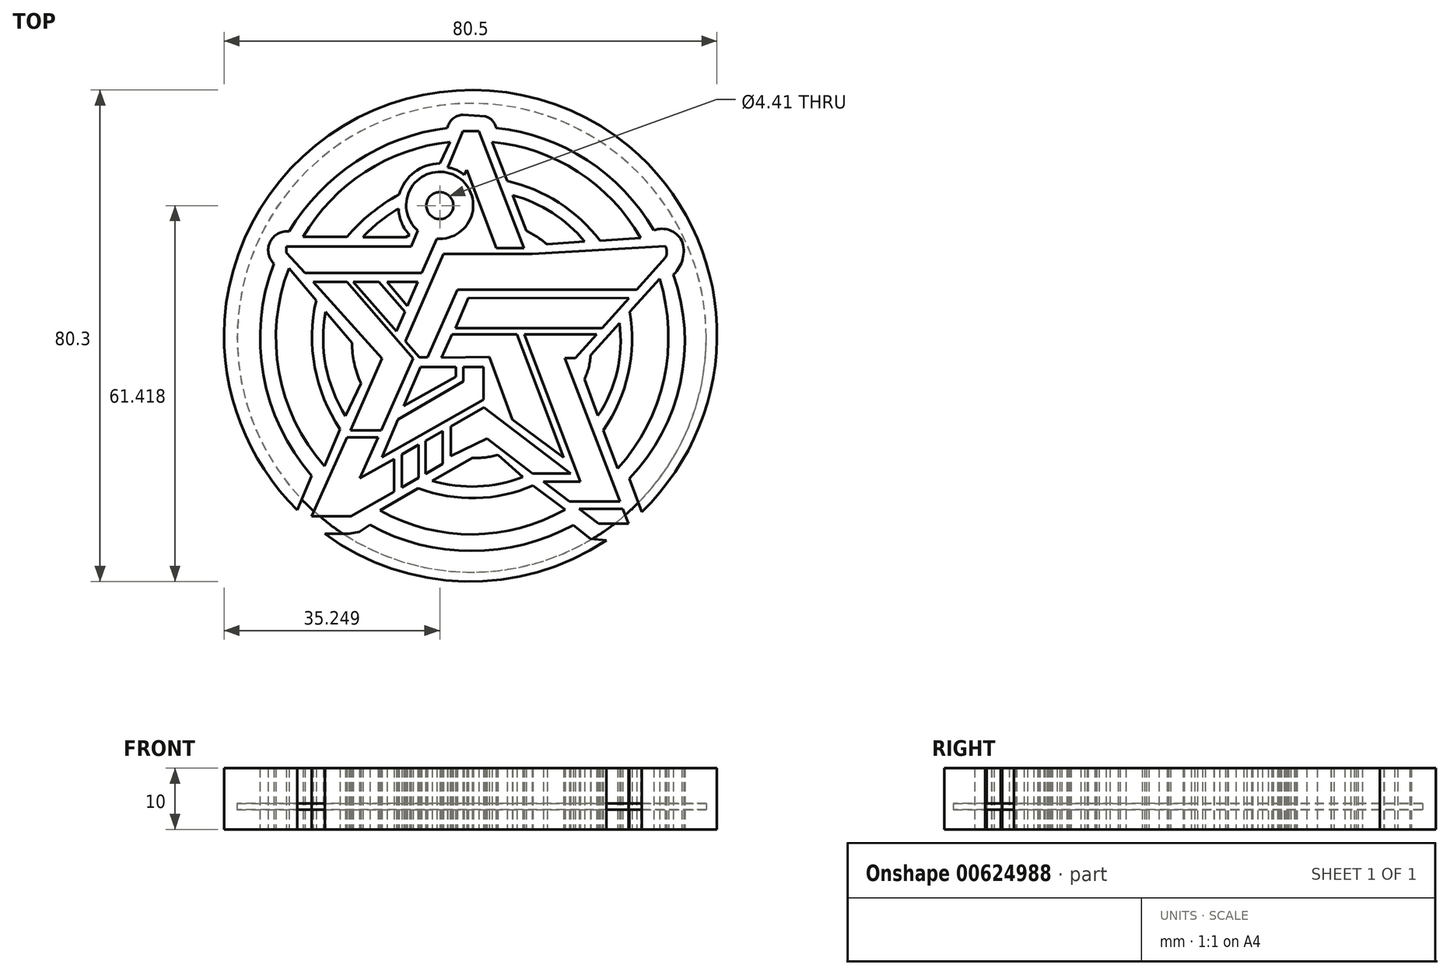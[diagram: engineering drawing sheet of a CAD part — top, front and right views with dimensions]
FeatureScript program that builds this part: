
annotation { "Feature Type Name" : "Feature", "Feature Type Description" : "" }
export const myFeature = defineFeature(function(context is Context, id is Id, definition is map)
    precondition{}
    {
        {
            var Q0;
            Q0=qCreatedBy(makeId("Top.planeOp"),FACE);
            var sketch = newSketch(context, id + "F0", { "sketchPlane" : qUnion([Q0])});
            skCircle(sketch, "E0", {"center": v(0, 0) * mm, "radius": 19.62 * mm, "construction": true});
            skCircle(sketch, "E1", {"center": v(0, 0) * mm, "radius": 24.24 * mm, "construction": true});
            skCircle(sketch, "E2", {"center": v(0, 0) * mm, "radius": 34.5 * mm, "construction": true});
            skLineSegment(sketch, "E3", {"start": v(20.7, -30.4) * mm, "end": v(2.49, -16.49) * mm, "construction": true});
            skLineSegment(sketch, "E4", {"start": v(2.49, -16.49) * mm, "end": v(-19.72, -29.2) * mm, "construction": true});
            skLineSegment(sketch, "E5", {"start": v(2, -11.38) * mm, "end": v(-18.24, -22.97) * mm, "construction": true});
            skLineSegment(sketch, "E6", {"start": v(-18.24, -22.97) * mm, "end": v(-9.56, -3.39) * mm, "construction": true});
            skLineSegment(sketch, "E7", {"start": v(-5.7, 16.2) * mm, "end": v(-12.28, 1.1) * mm, "construction": true});
            skLineSegment(sketch, "E8", {"start": v(-25.9, 9.11) * mm, "end": v(-8.79, 9.11) * mm, "construction": true});
            skLineSegment(sketch, "E9", {"start": v(23.83, -21.37) * mm, "end": v(18.4, -6.8) * mm, "construction": true});
            skLineSegment(sketch, "E10", {"start": v(30.66, 9.62) * mm, "end": v(19.42, -2.8) * mm, "construction": true});
            skLineSegment(sketch, "E11", {"start": v(25.58, -30.36) * mm, "end": v(15.19, -3.34) * mm, "construction": true});
            skLineSegment(sketch, "E12", {"start": v(15.19, -3.34) * mm, "end": v(16.91, -3.34) * mm, "construction": true});
            skLineSegment(sketch, "E13", {"start": v(16.91, -3.34) * mm, "end": v(31.66, 13.12) * mm, "construction": true});
            skLineSegment(sketch, "E14", {"start": v(27.56, 16.32) * mm, "end": v(12.3, 15.29) * mm, "construction": true});
            skLineSegment(sketch, "E15", {"start": v(3.31, 32) * mm, "end": v(8.9, 17.49) * mm, "construction": true});
            skArc(sketch, "E16", {"start": v(12.3, 15.29) * mm, "mid": v(10.66, 16.48) * mm, "end": v(8.9, 17.49) * mm});
            skArc(sketch, "E17", {"start": v(18.46, 15.7) * mm, "mid": v(13.15, 20.41) * mm, "end": v(6.66, 23.3) * mm});
            skArc(sketch, "E18", {"start": v(20.95, 15.87) * mm, "mid": v(14.22, 22.1) * mm, "end": v(5.77, 25.62) * mm});
            skArc(sketch, "E19", {"start": v(27.56, 16.32) * mm, "mid": v(17.36, 27.13) * mm, "end": v(3.31, 32) * mm});
            skLineSegment(sketch, "E20", {"start": v(3.31, 32) * mm, "end": v(5.77, 25.62) * mm});
            skLineSegment(sketch, "E21", {"start": v(6.66, 23.3) * mm, "end": v(8.9, 17.49) * mm});
            skLineSegment(sketch, "E22", {"start": v(12.3, 15.29) * mm, "end": v(18.46, 15.7) * mm});
            skLineSegment(sketch, "E23", {"start": v(20.95, 15.87) * mm, "end": v(27.56, 16.32) * mm});
            skLineSegment(sketch, "E24", {"start": v(-3.92, 27.8) * mm, "end": v(-1.42, 33.75) * mm});
            skLineSegment(sketch, "E25", {"start": v(-1.42, 33.75) * mm, "end": v(1.17, 33.75) * mm});
            skLineSegment(sketch, "E26", {"start": v(1.17, 33.75) * mm, "end": v(8.52, 14.66) * mm});
            skLineSegment(sketch, "E27", {"start": v(8.52, 14.66) * mm, "end": v(4.02, 14.66) * mm});
            skLineSegment(sketch, "E28", {"start": v(4.02, 14.66) * mm, "end": v(-0.78, 27.44) * mm});
            skLineSegment(sketch, "E29", {"start": v(-0.78, 27.44) * mm, "end": v(-1.24, 26.58) * mm});
            skArc(sketch, "E30", {"start": v(-1.24, 26.58) * mm, "mid": v(-2.48, 27.41) * mm, "end": v(-3.92, 27.8) * mm});
            skCircle(sketch, "E31", {"center": v(-5.21, 21.6) * mm, "radius": 2.2 * mm});
            skLineSegment(sketch, "E32", {"start": v(-5.7, 16.2) * mm, "end": v(-8.16, 10.56) * mm});
            skLineSegment(sketch, "E33", {"start": v(-8.16, 10.56) * mm, "end": v(-27.23, 10.56) * mm});
            skLineSegment(sketch, "E34", {"start": v(-27.23, 10.56) * mm, "end": v(-30.3, 13.9) * mm});
            skLineSegment(sketch, "E35", {"start": v(-30.3, 13.9) * mm, "end": v(-30.3, 14.9) * mm});
            skLineSegment(sketch, "E36", {"start": v(-30.3, 14.9) * mm, "end": v(-9.9, 14.9) * mm});
            skLineSegment(sketch, "E37", {"start": v(-9.9, 14.9) * mm, "end": v(-8.78, 17.49) * mm});
            skArc(sketch, "E38", {"start": v(-5.7, 16.2) * mm, "mid": v(-3.11, 26.69) * mm, "end": v(-8.78, 17.49) * mm});
            skLineSegment(sketch, "E39", {"start": v(-10.79, 16.46) * mm, "end": v(-10.16, 16.79) * mm});
            skLineSegment(sketch, "E40", {"start": v(-10.79, 16.46) * mm, "end": v(-17.8, 16.46) * mm});
            skArc(sketch, "E41", {"start": v(-11.95, 21.09) * mm, "mid": v(-15.04, 18.99) * mm, "end": v(-17.8, 16.46) * mm});
            skArc(sketch, "E42", {"start": v(-11.95, 21.09) * mm, "mid": v(-11.44, 18.78) * mm, "end": v(-10.16, 16.79) * mm});
            skArc(sketch, "E43", {"start": v(-5.2, 28.49) * mm, "mid": v(-9.36, 27.06) * mm, "end": v(-11.83, 23.42) * mm});
            skLineSegment(sketch, "E44", {"start": v(-5.2, 28.49) * mm, "end": v(-3.52, 32.02) * mm});
            skLineSegment(sketch, "E45", {"start": v(-20.38, 16.47) * mm, "end": v(-27.54, 16.47) * mm});
            skArc(sketch, "E46", {"start": v(-3.52, 32.02) * mm, "mid": v(-17.38, 27.1) * mm, "end": v(-27.54, 16.47) * mm});
            skArc(sketch, "E47", {"start": v(-11.83, 23.42) * mm, "mid": v(-16.43, 20.34) * mm, "end": v(-20.38, 16.47) * mm});
            skLineSegment(sketch, "E48", {"start": v(-13.82, 9.11) * mm, "end": v(-10.5, 5.18) * mm});
            skLineSegment(sketch, "E49", {"start": v(-10.5, 5.18) * mm, "end": v(-8.79, 9.11) * mm});
            skLineSegment(sketch, "E50", {"start": v(-13.82, 9.11) * mm, "end": v(-8.79, 9.11) * mm});
            skLineSegment(sketch, "E51", {"start": v(-19.38, 9.11) * mm, "end": v(-15.15, 9.11) * mm});
            skLineSegment(sketch, "E52", {"start": v(-15.15, 9.11) * mm, "end": v(-10.91, 4.22) * mm});
            skLineSegment(sketch, "E53", {"start": v(-10.91, 4.22) * mm, "end": v(-12.28, 1.1) * mm});
            skLineSegment(sketch, "E54", {"start": v(-12.28, 1.1) * mm, "end": v(-19.38, 9.11) * mm});
            skLineSegment(sketch, "E55", {"start": v(-25.9, 9.11) * mm, "end": v(-20.34, 9.11) * mm});
            skLineSegment(sketch, "E56", {"start": v(-20.34, 9.11) * mm, "end": v(-9.56, -3.39) * mm});
            skLineSegment(sketch, "E57", {"start": v(-9.56, -3.39) * mm, "end": v(-14.76, -15.11) * mm});
            skLineSegment(sketch, "E58", {"start": v(-14.76, -15.11) * mm, "end": v(-19.82, -15.11) * mm});
            skLineSegment(sketch, "E59", {"start": v(-19.82, -15.11) * mm, "end": v(-14.62, -3.39) * mm});
            skLineSegment(sketch, "E60", {"start": v(-14.62, -3.39) * mm, "end": v(-25.9, 9.11) * mm});
            skLineSegment(sketch, "E61", {"start": v(-7.25, -3.18) * mm, "end": v(-8.54, -3.18) * mm});
            skLineSegment(sketch, "E62", {"start": v(-8.54, -3.18) * mm, "end": v(-10.84, -0.58) * mm});
            skLineSegment(sketch, "E63", {"start": v(-10.84, -0.58) * mm, "end": v(-4.63, 13.7) * mm});
            skLineSegment(sketch, "E64", {"start": v(-4.63, 13.7) * mm, "end": v(9.88, 13.7) * mm});
            skLineSegment(sketch, "E65", {"start": v(9.88, 13.7) * mm, "end": v(31.6, 14.98) * mm});
            skLineSegment(sketch, "E66", {"start": v(31.66, 13.12) * mm, "end": v(26.93, 7.84) * mm});
            skLineSegment(sketch, "E67", {"start": v(26.93, 7.84) * mm, "end": v(-2.35, 7.84) * mm});
            skLineSegment(sketch, "E68", {"start": v(-2.35, 7.84) * mm, "end": v(-7.25, -3.18) * mm});
            skArc(sketch, "E69", {"start": v(31.66, 13.12) * mm, "mid": v(31.86, 14.06) * mm, "end": v(31.6, 14.98) * mm});
            skLineSegment(sketch, "E70", {"start": v(25.68, 6.44) * mm, "end": v(21.3, 1.56) * mm});
            skLineSegment(sketch, "E71", {"start": v(21.3, 1.56) * mm, "end": v(-2.63, 1.56) * mm});
            skLineSegment(sketch, "E72", {"start": v(-0.54, 6.55) * mm, "end": v(-4.93, -3.25) * mm, "construction": true});
            skLineSegment(sketch, "E73", {"start": v(1.9, -4.77) * mm, "end": v(-8.37, -4.77) * mm, "construction": true});
            skLineSegment(sketch, "E74", {"start": v(-8.37, -4.77) * mm, "end": v(-14.63, -19.5) * mm, "construction": true});
            skLineSegment(sketch, "E75", {"start": v(-11.07, -11.11) * mm, "end": v(-2.59, -6.39) * mm});
            skLineSegment(sketch, "E76", {"start": v(-2.59, -6.39) * mm, "end": v(-2.59, -4.77) * mm});
            skLineSegment(sketch, "E77", {"start": v(-2.59, -4.77) * mm, "end": v(-8.37, -4.77) * mm});
            skLineSegment(sketch, "E78", {"start": v(-11.07, -11.11) * mm, "end": v(-8.37, -4.77) * mm});
            skLineSegment(sketch, "E79", {"start": v(-1.37, -4.77) * mm, "end": v(1.9, -4.77) * mm});
            skLineSegment(sketch, "E80", {"start": v(1.9, -10.12) * mm, "end": v(1.9, -4.77) * mm});
            skLineSegment(sketch, "E81", {"start": v(1.9, -10.12) * mm, "end": v(-14.63, -19.5) * mm});
            skLineSegment(sketch, "E82", {"start": v(-1.37, -4.77) * mm, "end": v(-1.37, -7.1) * mm});
            skLineSegment(sketch, "E83", {"start": v(-1.37, -7.1) * mm, "end": v(-12.03, -13.38) * mm});
            skLineSegment(sketch, "E84", {"start": v(-12.03, -13.38) * mm, "end": v(-14.63, -19.5) * mm});
            skLineSegment(sketch, "E85", {"start": v(20.38, 0.53) * mm, "end": v(-3.24, 0.53) * mm, "construction": true});
            skLineSegment(sketch, "E86", {"start": v(-3.24, 0.53) * mm, "end": v(7.4, 0.53) * mm});
            skLineSegment(sketch, "E87", {"start": v(7.4, 0.53) * mm, "end": v(14.97, -19.6) * mm});
            skLineSegment(sketch, "E88", {"start": v(14.97, -19.6) * mm, "end": v(6.62, -13.36) * mm});
            skLineSegment(sketch, "E89", {"start": v(6.62, -13.36) * mm, "end": v(2.87, -3.12) * mm});
            skLineSegment(sketch, "E90", {"start": v(2.87, -3.12) * mm, "end": v(-4.93, -3.25) * mm});
            skLineSegment(sketch, "E91", {"start": v(-4.93, -3.25) * mm, "end": v(-3.24, 0.53) * mm});
            skLineSegment(sketch, "E92", {"start": v(20.38, 0.53) * mm, "end": v(8.57, 0.53) * mm});
            skLineSegment(sketch, "E93", {"start": v(8.57, 0.53) * mm, "end": v(17.74, -23.52) * mm});
            skLineSegment(sketch, "E94", {"start": v(17.74, -23.52) * mm, "end": v(11.7, -23.52) * mm});
            skLineSegment(sketch, "E95", {"start": v(11.7, -23.52) * mm, "end": v(15.95, -26.77) * mm});
            skLineSegment(sketch, "E96", {"start": v(15.95, -26.77) * mm, "end": v(24.2, -26.77) * mm});
            skLineSegment(sketch, "E97", {"start": v(24.2, -26.77) * mm, "end": v(15.19, -3.34) * mm});
            skLineSegment(sketch, "E98", {"start": v(15.19, -3.34) * mm, "end": v(16.91, -3.34) * mm});
            skLineSegment(sketch, "E99", {"start": v(16.91, -3.34) * mm, "end": v(20.38, 0.53) * mm});
            skLineSegment(sketch, "E100", {"start": v(-2.63, 1.56) * mm, "end": v(-0.54, 6.55) * mm});
            skLineSegment(sketch, "E101", {"start": v(-0.54, 6.55) * mm, "end": v(25.68, 6.44) * mm});
            skArc(sketch, "E102", {"start": v(18.4, -6.8) * mm, "mid": v(19.1, -4.85) * mm, "end": v(19.42, -2.8) * mm});
            skArc(sketch, "E103", {"start": v(20.62, -12.74) * mm, "mid": v(23.74, -5.5) * mm, "end": v(24.12, 2.38) * mm});
            skArc(sketch, "E104", {"start": v(21.5, -15.12) * mm, "mid": v(25.55, -5.86) * mm, "end": v(25.8, 4.24) * mm});
            skArc(sketch, "E105", {"start": v(23.83, -21.37) * mm, "mid": v(31.37, -6.79) * mm, "end": v(30.66, 9.62) * mm});
            skLineSegment(sketch, "E106", {"start": v(30.66, 9.62) * mm, "end": v(25.8, 4.24) * mm});
            skLineSegment(sketch, "E107", {"start": v(24.12, 2.38) * mm, "end": v(19.42, -2.8) * mm});
            skLineSegment(sketch, "E108", {"start": v(18.4, -6.8) * mm, "end": v(20.62, -12.74) * mm});
            skLineSegment(sketch, "E109", {"start": v(21.5, -15.12) * mm, "end": v(23.83, -21.37) * mm});
            skLineSegment(sketch, "E110", {"start": v(17.52, -27.97) * mm, "end": v(24.66, -27.97) * mm});
            skLineSegment(sketch, "E111", {"start": v(24.66, -27.97) * mm, "end": v(25.58, -30.36) * mm});
            skLineSegment(sketch, "E112", {"start": v(25.58, -30.36) * mm, "end": v(20.7, -30.4) * mm});
            skLineSegment(sketch, "E113", {"start": v(20.7, -30.4) * mm, "end": v(17.52, -27.97) * mm});
            skArc(sketch, "E114", {"start": v(0, -19.62) * mm, "mid": v(2.16, -19.55) * mm, "end": v(4.29, -19.15) * mm});
            skArc(sketch, "E115", {"start": v(-6.43, -23.37) * mm, "mid": v(1, -24.3) * mm, "end": v(8.3, -22.77) * mm});
            skArc(sketch, "E116", {"start": v(-8.72, -24.58) * mm, "mid": v(0.68, -26.2) * mm, "end": v(10, -24.17) * mm});
            skArc(sketch, "E117", {"start": v(-14.96, -28.23) * mm, "mid": v(0.19, -32.12) * mm, "end": v(15.28, -28.06) * mm});
            skLineSegment(sketch, "E118", {"start": v(15.28, -28.06) * mm, "end": v(10, -24.17) * mm});
            skLineSegment(sketch, "E119", {"start": v(8.3, -22.77) * mm, "end": v(4.29, -19.15) * mm});
            skLineSegment(sketch, "E120", {"start": v(-6.43, -23.37) * mm, "end": v(0.1, -19.62) * mm});
            skLineSegment(sketch, "E121", {"start": v(-8.72, -24.58) * mm, "end": v(-14.96, -28.23) * mm});
            skLineSegment(sketch, "E122", {"start": v(-3.41, -19.32) * mm, "end": v(-3.41, -14.49) * mm});
            skLineSegment(sketch, "E123", {"start": v(-3.41, -14.49) * mm, "end": v(2, -11.38) * mm});
            skLineSegment(sketch, "E124", {"start": v(2, -11.38) * mm, "end": v(16.13, -22.15) * mm});
            skLineSegment(sketch, "E125", {"start": v(16.13, -22.15) * mm, "end": v(9.9, -22.15) * mm});
            skLineSegment(sketch, "E126", {"start": v(9.9, -22.15) * mm, "end": v(2.49, -16.49) * mm});
            skLineSegment(sketch, "E127", {"start": v(2.49, -16.49) * mm, "end": v(-3.41, -19.32) * mm});
            skLineSegment(sketch, "E128", {"start": v(-4.73, -15.24) * mm, "end": v(-4.73, -20.62) * mm});
            skLineSegment(sketch, "E129", {"start": v(-4.73, -20.62) * mm, "end": v(-7.57, -22.25) * mm});
            skLineSegment(sketch, "E130", {"start": v(-7.57, -22.25) * mm, "end": v(-7.57, -16.87) * mm});
            skLineSegment(sketch, "E131", {"start": v(-7.57, -16.87) * mm, "end": v(-4.73, -15.24) * mm});
            skLineSegment(sketch, "E132", {"start": v(-8.7, -17.5) * mm, "end": v(-8.7, -22.89) * mm});
            skLineSegment(sketch, "E133", {"start": v(-8.7, -22.89) * mm, "end": v(-11.42, -24.45) * mm});
            skLineSegment(sketch, "E134", {"start": v(-11.42, -24.45) * mm, "end": v(-11.42, -19.07) * mm});
            skLineSegment(sketch, "E135", {"start": v(-11.42, -19.07) * mm, "end": v(-8.7, -17.5) * mm});
            skLineSegment(sketch, "E136", {"start": v(-12.7, -19.8) * mm, "end": v(-12.7, -25.18) * mm});
            skLineSegment(sketch, "E137", {"start": v(-12.7, -25.18) * mm, "end": v(-19.72, -29.2) * mm});
            skLineSegment(sketch, "E138", {"start": v(-26.12, -29.2) * mm, "end": v(-20.34, -16.27) * mm});
            skLineSegment(sketch, "E139", {"start": v(-20.34, -16.27) * mm, "end": v(-15.27, -16.27) * mm});
            skLineSegment(sketch, "E140", {"start": v(-15.27, -16.27) * mm, "end": v(-18.24, -22.97) * mm});
            skLineSegment(sketch, "E141", {"start": v(-18.24, -22.97) * mm, "end": v(-12.7, -19.8) * mm});
            skLineSegment(sketch, "E142", {"start": v(-18.24, -7.23) * mm, "end": v(-24.08, -20.94) * mm, "construction": true});
            skLineSegment(sketch, "E143", {"start": v(-19.57, -0.83) * mm, "end": v(-29.85, 11.36) * mm, "construction": true});
            skArc(sketch, "E144", {"start": v(-19.57, -0.83) * mm, "mid": v(-19.18, -4.21) * mm, "end": v(-18.1, -7.44) * mm});
            skArc(sketch, "E145", {"start": v(-23.86, 4.26) * mm, "mid": v(-23.85, -4.56) * mm, "end": v(-20.6, -12.77) * mm});
            skArc(sketch, "E146", {"start": v(-25.4, 6.09) * mm, "mid": v(-25.63, -4.81) * mm, "end": v(-21.51, -14.9) * mm});
            skArc(sketch, "E147", {"start": v(-29.85, 11.36) * mm, "mid": v(-31.47, -5.6) * mm, "end": v(-24.08, -20.94) * mm});
            skLineSegment(sketch, "E148", {"start": v(-19.57, -0.83) * mm, "end": v(-23.86, 4.26) * mm});
            skLineSegment(sketch, "E149", {"start": v(-25.4, 6.09) * mm, "end": v(-29.85, 11.36) * mm});
            skLineSegment(sketch, "E150", {"start": v(-18.1, -7.44) * mm, "end": v(-20.6, -12.77) * mm});
            skLineSegment(sketch, "E151", {"start": v(-21.51, -14.9) * mm, "end": v(-24.08, -20.94) * mm});
            skPoint(sketch, "E152.endSnap0", {"position": v(-25.63, -4.81) * mm});
            skArc(sketch, "E153", {"start": v(25.72, -23) * mm, "mid": v(34.06, -7.35) * mm, "end": v(32.92, 10.35) * mm});
            skArc(sketch, "E154", {"start": v(29.71, 17.55) * mm, "mid": v(18.86, 29.01) * mm, "end": v(3.98, 34.28) * mm});
            skArc(sketch, "E155", {"start": v(-3.98, 34.28) * mm, "mid": v(-18.86, 28.81) * mm, "end": v(-29.82, 17.37) * mm});
            skArc(sketch, "E156", {"start": v(-29.82, 17.37) * mm, "mid": v(-32.94, 15.64) * mm, "end": v(-32.3, 12.14) * mm});
            skArc(sketch, "E157", {"start": v(-1.42, 36.44) * mm, "mid": v(-3.07, 35.8) * mm, "end": v(-3.98, 34.28) * mm});
            skArc(sketch, "E158", {"start": v(3.98, 34.28) * mm, "mid": v(3.36, 35.48) * mm, "end": v(2.22, 36.2) * mm});
            skLineSegment(sketch, "E159", {"start": v(2.22, 36.2) * mm, "end": v(-1.42, 36.44) * mm});
            skArc(sketch, "E160", {"start": v(34.3, 15.87) * mm, "mid": v(32.32, 17.57) * mm, "end": v(29.71, 17.55) * mm});
            skArc(sketch, "E161", {"start": v(32.92, 10.35) * mm, "mid": v(34.45, 12.9) * mm, "end": v(34.3, 15.87) * mm});
            skLineSegment(sketch, "E162", {"start": v(25.72, -23) * mm, "end": v(27.79, -28.43) * mm});
            skLineSegment(sketch, "E163", {"start": v(19.4, -32.85) * mm, "end": v(21.95, -33.13) * mm});
            skLineSegment(sketch, "E164", {"start": v(-18.36, -31.69) * mm, "end": v(-20.07, -32.03) * mm});
            skLineSegment(sketch, "E165", {"start": v(-20.07, -32.03) * mm, "end": v(-24.02, -32.03) * mm});
            skArc(sketch, "E166", {"start": v(-32.3, 12.14) * mm, "mid": v(-34.03, -6.06) * mm, "end": v(-26.13, -22.54) * mm});
            skLineSegment(sketch, "E167", {"start": v(-26.13, -22.54) * mm, "end": v(-28.48, -28.16) * mm});
            skArc(sketch, "E168", {"start": v(27.79, -28.43) * mm, "mid": v(0, 40.74) * mm, "end": v(-28.48, -28.16) * mm});
            skArc(sketch, "E169", {"start": v(-16.63, -30.59) * mm, "mid": v(-0.02, -34.84) * mm, "end": v(16.59, -30.6) * mm});
            skLineSegment(sketch, "E170", {"start": v(19.4, -32.85) * mm, "end": v(16.59, -30.6) * mm});
            skLineSegment(sketch, "E171", {"start": v(-18.36, -31.69) * mm, "end": v(-16.63, -30.59) * mm});
            skArc(sketch, "E172", {"start": v(-24.02, -32.03) * mm, "mid": v(-1.2, -39.8) * mm, "end": v(21.95, -33.13) * mm});
            skCircle(sketch, "E173", {"center": v(0.01, -0.03) * mm, "radius": 40.5 * mm});
            skCircle(sketch, "E174", {"center": v(0.01, -0.03) * mm, "radius": 41.57 * mm});
            skLineSegment(sketch, "E175", {"start": v(-19.72, -29.2) * mm, "end": v(-26.12, -29.2) * mm});
            skSolve(sketch);
        }
        {
            var Q0;
            Q0=makeQuery(id+"F0.imprint","IMPRINT",FACE,{"disambiguationData":[TD([[makeQuery(id+"F0.imprint","IMPRINT",EDGE,{"derivedFrom":sQuery(id+"F0.wireOp",EDGE,"E31")}),-1.0]])]});
            var Q1;
            Q1=makeQuery(id+"F0.imprint","IMPRINT",FACE,{"disambiguationData":[TD([[makeQuery(id+"F0.imprint","IMPRINT",EDGE,{"derivedFrom":sQuery(id+"F0.wireOp",EDGE,"E39")}),1.0]])]});
            var Q2;
            Q2=makeQuery(id+"F0.imprint","IMPRINT",FACE,{"disambiguationData":[TD([[makeQuery(id+"F0.imprint","IMPRINT",EDGE,{"derivedFrom":sQuery(id+"F0.wireOp",EDGE,"E43")}),-1.0]])]});
            var Q3;
            Q3=makeQuery(id+"F0.imprint","IMPRINT",FACE,{"disambiguationData":[TD([[makeQuery(id+"F0.imprint","IMPRINT",EDGE,{"derivedFrom":sQuery(id+"F0.wireOp",EDGE,"E24")}),-1.0]])]});
            var Q4;
            Q4=makeQuery(id+"F0.imprint","IMPRINT",FACE,{"disambiguationData":[TD([[makeQuery(id+"F0.imprint","IMPRINT",EDGE,{"derivedFrom":sQuery(id+"F0.wireOp",EDGE,"E18")}),-1.0]])]});
            var Q5;
            Q5=makeQuery(id+"F0.imprint","IMPRINT",FACE,{"disambiguationData":[TD([[makeQuery(id+"F0.imprint","IMPRINT",EDGE,{"derivedFrom":sQuery(id+"F0.wireOp",EDGE,"E16")}),-1.0]])]});
            var Q6;
            Q6=makeQuery(id+"F0.imprint","IMPRINT",FACE,{"disambiguationData":[TD([[makeQuery(id+"F0.imprint","IMPRINT",EDGE,{"derivedFrom":sQuery(id+"F0.wireOp",EDGE,"E61")}),-1.0]])]});
            var Q7;
            Q7=makeQuery(id+"F0.imprint","IMPRINT",FACE,{"disambiguationData":[TD([[makeQuery(id+"F0.imprint","IMPRINT",EDGE,{"derivedFrom":sQuery(id+"F0.wireOp",EDGE,"E70")}),-1.0]])]});
            var Q8;
            Q8=makeQuery(id+"F0.imprint","IMPRINT",FACE,{"disambiguationData":[TD([[makeQuery(id+"F0.imprint","IMPRINT",EDGE,{"derivedFrom":sQuery(id+"F0.wireOp",EDGE,"E48")}),1.0]])]});
            var Q9;
            Q9=makeQuery(id+"F0.imprint","IMPRINT",FACE,{"disambiguationData":[TD([[makeQuery(id+"F0.imprint","IMPRINT",EDGE,{"derivedFrom":sQuery(id+"F0.wireOp",EDGE,"E51")}),-1.0]])]});
            var Q10;
            Q10=makeQuery(id+"F0.imprint","IMPRINT",FACE,{"disambiguationData":[TD([[makeQuery(id+"F0.imprint","IMPRINT",EDGE,{"derivedFrom":sQuery(id+"F0.wireOp",EDGE,"E55")}),-1.0]])]});
            var Q11;
            Q11=makeQuery(id+"F0.imprint","IMPRINT",FACE,{"disambiguationData":[TD([[makeQuery(id+"F0.imprint","IMPRINT",EDGE,{"derivedFrom":sQuery(id+"F0.wireOp",EDGE,"E75")}),1.0]])]});
            var Q12;
            Q12=makeQuery(id+"F0.imprint","IMPRINT",FACE,{"disambiguationData":[TD([[makeQuery(id+"F0.imprint","IMPRINT",EDGE,{"derivedFrom":sQuery(id+"F0.wireOp",EDGE,"E79")}),-1.0]])]});
            var Q13;
            Q13=makeQuery(id+"F0.imprint","IMPRINT",FACE,{"disambiguationData":[TD([[makeQuery(id+"F0.imprint","IMPRINT",EDGE,{"derivedFrom":sQuery(id+"F0.wireOp",EDGE,"E86")}),-1.0]])]});
            var Q14;
            Q14=makeQuery(id+"F0.imprint","IMPRINT",FACE,{"disambiguationData":[TD([[makeQuery(id+"F0.imprint","IMPRINT",EDGE,{"derivedFrom":sQuery(id+"F0.wireOp",EDGE,"E92")}),1.0]])]});
            var Q15;
            Q15=makeQuery(id+"F0.imprint","IMPRINT",FACE,{"disambiguationData":[TD([[makeQuery(id+"F0.imprint","IMPRINT",EDGE,{"derivedFrom":sQuery(id+"F0.wireOp",EDGE,"E102")}),-1.0]])]});
            var Q16;
            Q16=makeQuery(id+"F0.imprint","IMPRINT",FACE,{"disambiguationData":[TD([[makeQuery(id+"F0.imprint","IMPRINT",EDGE,{"derivedFrom":sQuery(id+"F0.wireOp",EDGE,"E104")}),-1.0]])]});
            var Q17;
            Q17=makeQuery(id+"F0.imprint","IMPRINT",FACE,{"disambiguationData":[TD([[makeQuery(id+"F0.imprint","IMPRINT",EDGE,{"derivedFrom":sQuery(id+"F0.wireOp",EDGE,"E153")}),-1.0]])]});
            var Q18;
            Q18=makeQuery(id+"F0.imprint","IMPRINT",FACE,{"disambiguationData":[TD([[makeQuery(id+"F0.imprint","IMPRINT",EDGE,{"derivedFrom":sQuery(id+"F0.wireOp",EDGE,"E110")}),-1.0]])]});
            var Q19;
            Q19=makeQuery(id+"F0.imprint","IMPRINT",FACE,{"disambiguationData":[TD([[makeQuery(id+"F0.imprint","IMPRINT",EDGE,{"derivedFrom":sQuery(id+"F0.wireOp",EDGE,"E116")}),-1.0]])]});
            var Q20;
            Q20=makeQuery(id+"F0.imprint","IMPRINT",FACE,{"disambiguationData":[TD([[makeQuery(id+"F0.imprint","IMPRINT",EDGE,{"derivedFrom":sQuery(id+"F0.wireOp",EDGE,"E163")}),-1.0]])]});
            var Q21;
            {var subQ4=sQuery(id+"F0.wireOp",EDGE,"E115");Q21=makeQuery(id+"F0.imprint","IMPRINT",FACE,{"disambiguationData":[TD([[makeQuery(id+"F0.imprint","IMPRINT",EDGE,{"derivedFrom":subQ4}),1.0]])]});}
            var Q22;
            Q22=makeQuery(id+"F0.imprint","IMPRINT",FACE,{"disambiguationData":[TD([[makeQuery(id+"F0.imprint","IMPRINT",EDGE,{"derivedFrom":sQuery(id+"F0.wireOp",EDGE,"E122")}),-1.0]])]});
            var Q23;
            Q23=makeQuery(id+"F0.imprint","IMPRINT",FACE,{"disambiguationData":[TD([[makeQuery(id+"F0.imprint","IMPRINT",EDGE,{"derivedFrom":sQuery(id+"F0.wireOp",EDGE,"E128")}),-1.0]])]});
            var Q24;
            Q24=makeQuery(id+"F0.imprint","IMPRINT",FACE,{"disambiguationData":[TD([[makeQuery(id+"F0.imprint","IMPRINT",EDGE,{"derivedFrom":sQuery(id+"F0.wireOp",EDGE,"E132")}),-1.0]])]});
            var Q25;
            Q25=makeQuery(id+"F0.imprint","IMPRINT",FACE,{"disambiguationData":[TD([[makeQuery(id+"F0.imprint","IMPRINT",EDGE,{"derivedFrom":sQuery(id+"F0.wireOp",EDGE,"E144")}),-1.0]])]});
            var Q26;
            Q26=makeQuery(id+"F0.imprint","IMPRINT",FACE,{"disambiguationData":[TD([[makeQuery(id+"F0.imprint","IMPRINT",EDGE,{"derivedFrom":sQuery(id+"F0.wireOp",EDGE,"E146")}),-1.0]])]});
            var Q27;
            Q27=makeQuery(id+"F0.imprint","IMPRINT",FACE,{"disambiguationData":[TD([[makeQuery(id+"F0.imprint","IMPRINT",EDGE,{"derivedFrom":sQuery(id+"F0.wireOp",EDGE,"E136")}),-1.0]])]});
            extrude(context, id + "F1", {"entities" : qUnion([Q0, Q1, Q2, Q3, Q4, Q5, Q6, Q7, Q8, Q9, Q10, Q11, Q12, Q13, Q14, Q15, Q16, Q17, Q18, Q19, Q20, Q21, Q22, Q23, Q24, Q25, Q26, Q27]), "depth" : 10 * mm, "offsetDistance" : 25 * mm});
        }
        {
            var Q0;
            Q0=qCreatedBy(makeId("Top.planeOp"),FACE);
            var sketch = newSketch(context, id + "F2", { "sketchPlane" : qUnion([Q0])});
            skCircle(sketch, "E176", {"center": v(0, 0) * mm, "radius": 38.3 * mm});
            skSolve(sketch);
        }
        {
            var Q0;
            Q0=makeQuery(id+"F2.imprint","IMPRINT",FACE,{"disambiguationData":[TD([[makeQuery(id+"F2.imprint","IMPRINT",EDGE,{"derivedFrom":sQuery(id+"F2.wireOp",EDGE,"E176")}),1.0]])]});
            extrude(context, id + "F3", {"entities" : qUnion([Q0]), "depth" : 1 * mm, "offsetDistance" : 25 * mm});
        }
        {
            var Q0;
            Q0=makeQuery(id+"F3.opExtrude","SWEPT_BODY",BODY,{"disambiguationData":[OSD([sQuery(id+"F2.wireOp",EDGE,"E176")])]});
            transform(context, id + "F4", {"entities" : qUnion([Q0]), "transformType" : TransformType.TRANSLATION_3D, "dx" : 0 * mm, "dy" : 0 * mm, "dz" : 3.2 * mm, "makeCopy" : false});
        }
    });
